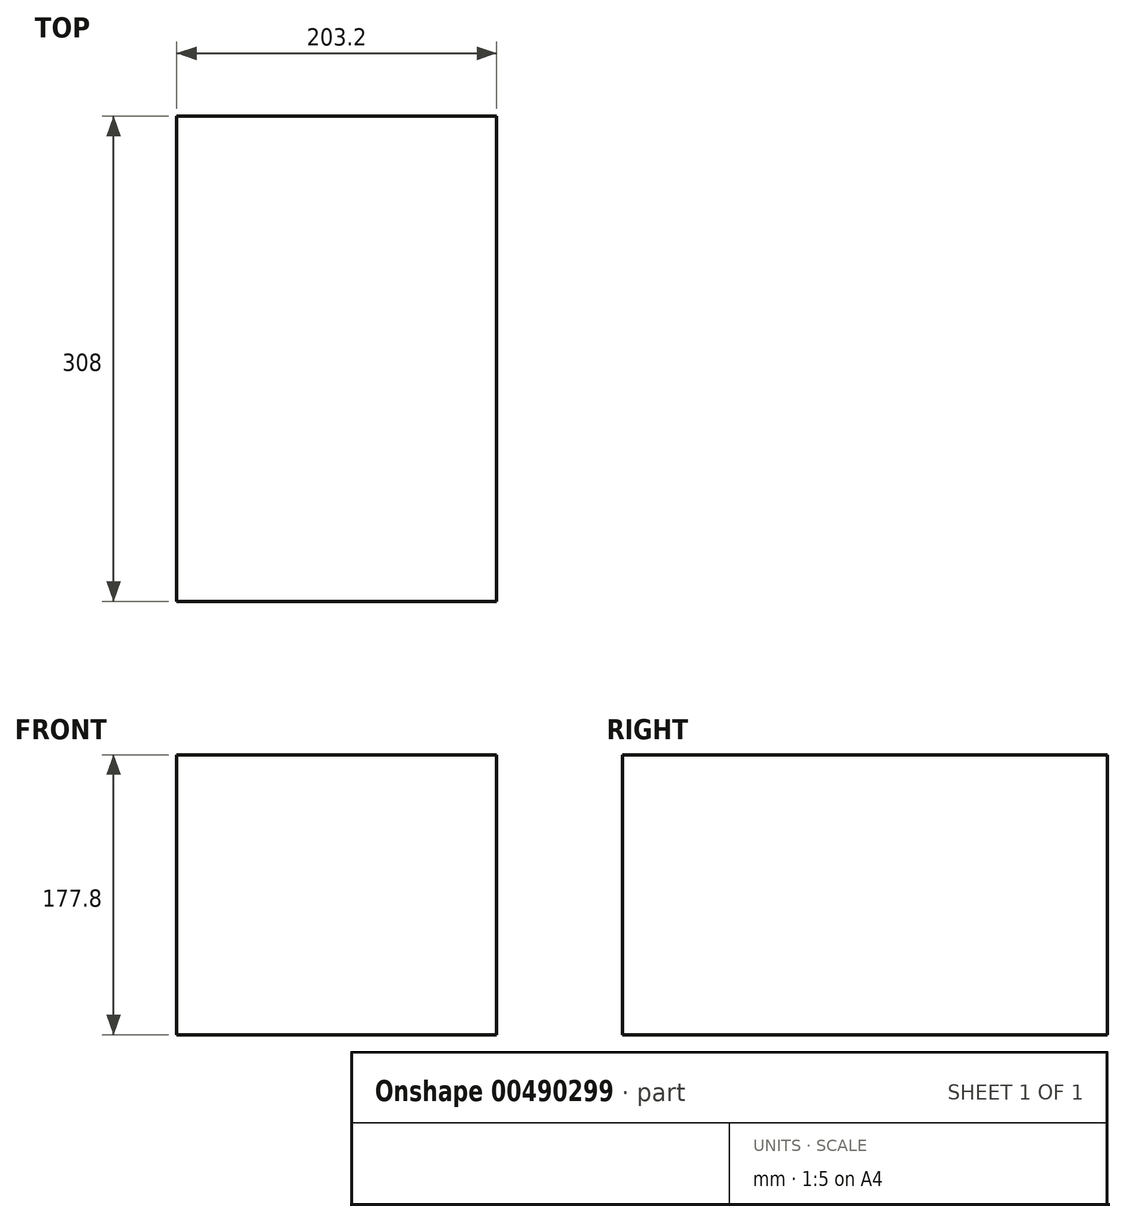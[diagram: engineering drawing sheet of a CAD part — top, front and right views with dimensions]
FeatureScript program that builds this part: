
annotation { "Feature Type Name" : "Feature", "Feature Type Description" : "" }
export const myFeature = defineFeature(function(context is Context, id is Id, definition is map)
    precondition{}
    {
        {
            var Q0;
            Q0=qCreatedBy(makeId("Top.planeOp"),FACE);
            var sketch = newSketch(context, id + "F0", { "sketchPlane" : qUnion([Q0])});
            skLineSegment(sketch, "E0.bottom", {"start": v(-101.6, 154) * mm, "end": v(101.6, 154) * mm});
            skLineSegment(sketch, "E0.top", {"start": v(-101.6, -154) * mm, "end": v(101.6, -154) * mm});
            skLineSegment(sketch, "E0.left", {"start": v(-101.6, 154) * mm, "end": v(-101.6, -154) * mm});
            skLineSegment(sketch, "E0.right", {"start": v(101.6, 154) * mm, "end": v(101.6, -154) * mm});
            skPoint(sketch, "E0.middle", {"position": v(0, 0) * mm});
            skSolve(sketch);
        }
        {
            var Q0;
            Q0 = qSketchRegion(id + "F0", true);
            extrude(context, id + "F1", {"entities" : qUnion([Q0]), "depth" : 177.8 * mm, "offsetDistance" : 25 * mm});
        }
    });
